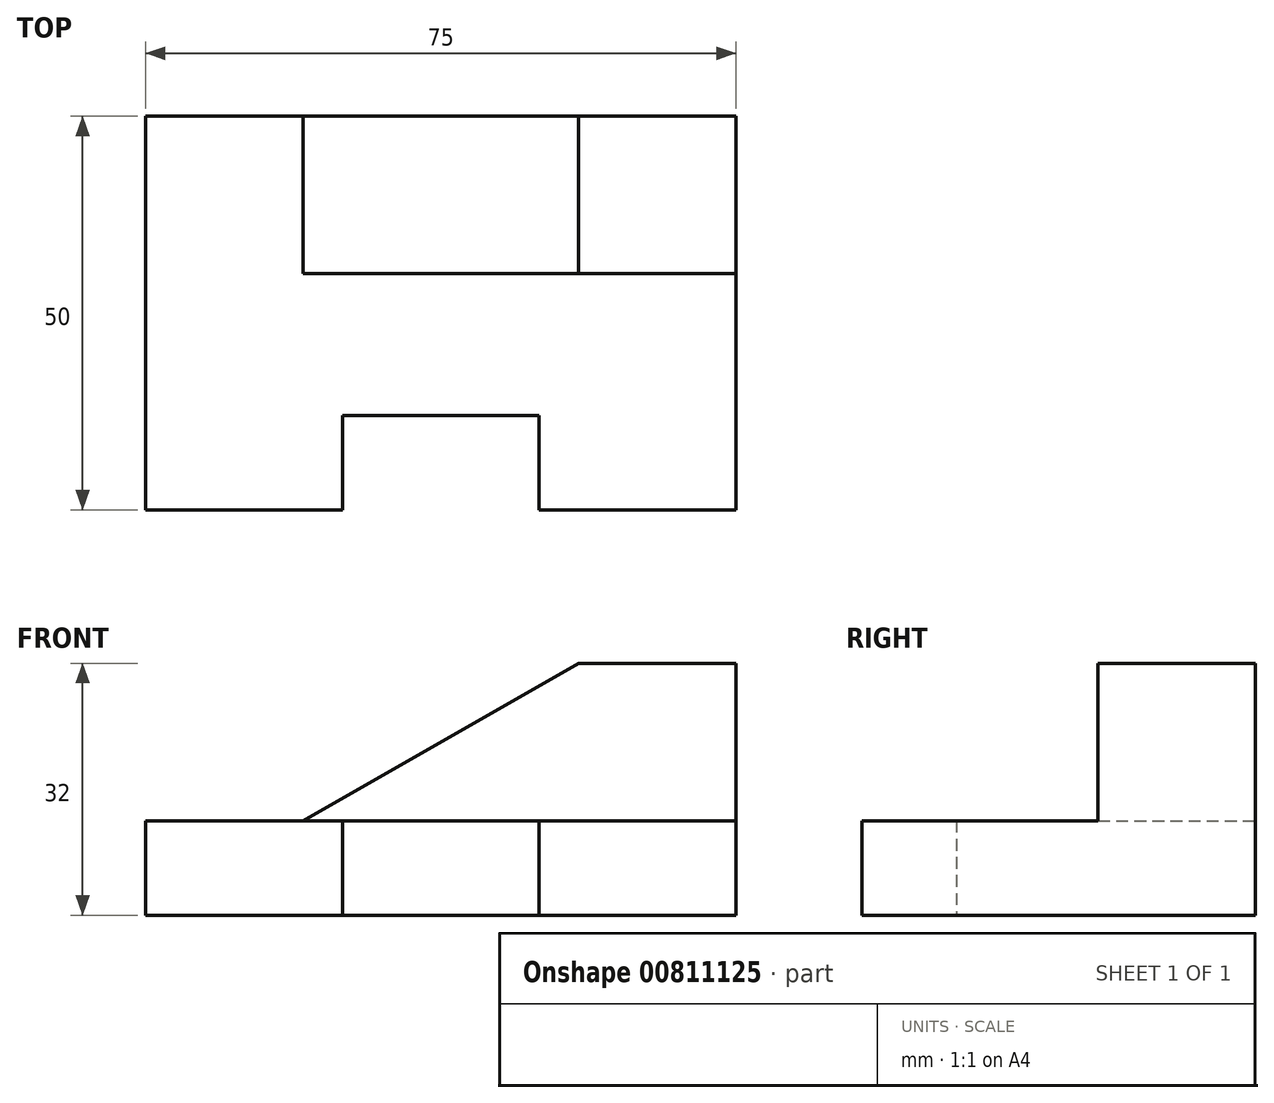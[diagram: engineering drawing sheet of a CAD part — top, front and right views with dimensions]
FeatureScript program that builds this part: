
annotation { "Feature Type Name" : "Feature", "Feature Type Description" : "" }
export const myFeature = defineFeature(function(context is Context, id is Id, definition is map)
    precondition{}
    {
        {
            var Q0;
            Q0=qCreatedBy(makeId("Top.planeOp"),FACE);
            var sketch = newSketch(context, id + "F0", { "sketchPlane" : qUnion([Q0])});
            skLineSegment(sketch, "E0.bottom", {"start": v(-37.5, 25) * mm, "end": v(37.5, 25) * mm});
            skLineSegment(sketch, "E0.top", {"start": v(-37.5, -25) * mm, "end": v(-12.5, -25) * mm});
            skLineSegment(sketch, "E0.left", {"start": v(-37.5, 25) * mm, "end": v(-37.5, -25) * mm});
            skLineSegment(sketch, "E0.right", {"start": v(37.5, 25) * mm, "end": v(37.5, -25) * mm});
            skPoint(sketch, "E0.middle", {"position": v(0, 0) * mm});
            skLineSegment(sketch, "E1", {"start": v(-12.5, -25) * mm, "end": v(-12.5, -13) * mm});
            skLineSegment(sketch, "E2", {"start": v(-12.5, -13) * mm, "end": v(12.5, -13) * mm});
            skLineSegment(sketch, "E3", {"start": v(12.5, -13) * mm, "end": v(12.5, -25) * mm});
            skLineSegment(sketch, "E4.trimOffspring", {"start": v(12.5, -25) * mm, "end": v(37.5, -25) * mm});
            skSolve(sketch);
        }
        {
            var Q0;
            Q0 = qSketchRegion(id + "F0", true);
            extrude(context, id + "F1", {"entities" : qUnion([Q0]), "depth" : 12 * mm, "offsetDistance" : 25 * mm});
        }
        {
            var Q0;
            Q0=makeQuery(id+"F1.opExtrude","CAP_FACE",FACE,{"disambiguationData":[OSD([sQuery(id+"F0.wireOp",EDGE,"E0.bottom"),sQuery(id+"F0.wireOp",EDGE,"E0.top"),sQuery(id+"F0.wireOp",EDGE,"E0.left"),sQuery(id+"F0.wireOp",EDGE,"E0.right"),sQuery(id+"F0.wireOp",EDGE,"E1"),sQuery(id+"F0.wireOp",EDGE,"E2"),sQuery(id+"F0.wireOp",EDGE,"E3"),sQuery(id+"F0.wireOp",EDGE,"E4.trimOffspring")])],"isStart":false});
            var sketch = newSketch(context, id + "F2", { "sketchPlane" : qUnion([Q0])});
            skLineSegment(sketch, "E5", {"start": v(37.5, 25) * mm, "end": v(37.5, 5) * mm});
            skLineSegment(sketch, "E6", {"start": v(37.5, 5) * mm, "end": v(-17.5, 5) * mm});
            skLineSegment(sketch, "E7", {"start": v(-17.5, 5) * mm, "end": v(-17.5, 25) * mm});
            skLineSegment(sketch, "E8", {"start": v(-17.5, 25) * mm, "end": v(37.5, 25) * mm});
            skSolve(sketch);
        }
        {
            var Q0;
            Q0 = qSketchRegion(id + "F2", true);
            extrude(context, id + "F3", {"entities" : qUnion([Q0]), "operationType" : NewBodyOperationType.ADD, "depth" : 20 * mm, "offsetDistance" : 25 * mm});
        }
        {
            var Q0;
            Q0=makeQuery(id+"F3.opExtrude","SWEPT_FACE",FACE,{"disambiguationData":[OSD([sQuery(id+"F2.wireOp",EDGE,"E6")])]});
            var sketch = newSketch(context, id + "F4", { "sketchPlane" : qUnion([Q0])});
            skLineSegment(sketch, "E9", {"start": v(37.5, 32) * mm, "end": v(17.5, 32) * mm, "construction": true});
            skLineSegment(sketch, "E10", {"start": v(17.5, 32) * mm, "end": v(-17.5, 12) * mm});
            skLineSegment(sketch, "E11", {"start": v(-17.5, 12) * mm, "end": v(-17.5, 32) * mm});
            skLineSegment(sketch, "E12", {"start": v(-17.5, 32) * mm, "end": v(17.5, 32) * mm});
            skSolve(sketch);
        }
        {
            var Q0;
            Q0 = qSketchRegion(id + "F4", true);
            extrude(context, id + "F5", {"entities" : qUnion([Q0]), "operationType" : NewBodyOperationType.REMOVE, "oppositeDirection" : true, "depth" : 25 * mm, "offsetDistance" : 25 * mm});
        }
    });
